# Revit family: ledlima_l15-36w-4000-dali-em1_549004003100
name_source: partatom
category: Leuchten
revit_build: Autodesk Revit 2016 (Build: 20190508_0715(x64)
units: mm (PartAtom-declared; Revit-internal decimal feet)

## family parameters
Basisbauteil = Fläche
Beim Laden mit Abzugskörper schneiden = Nein
Bemaßung runder Anschluss = Durchmesser verwenden
Gemeinsam genutzt = Nein
Lichtquelle = Nein
Raumberechnungspunkt = Nein
Teiletyp = Normal

## types (1)
- LEDLima L15-36W-4000-DALI-EM1 (1 x LED, 4140 lm)
    Approval mark = CE, ENEC
    Beschreibung = Stylish linear luminaire with high quality aluminum housing, suitable for surface mounting and suspended use. Suitable for use in office. Suspension kit including transparent cable as accessory. Connection kit accessory to create continuous lines available.
    CIE Flux Codes = 68 91 98 100 100
    Control Gear = Electronic ballast
    Height = 70 mm
    Hersteller = OPPLE
    Lamp Light Flux = 4140 lm
    Lamp count = 1
    Lampe = 1 x LED
    Length = 1500 mm
    Luminous efficacy = 115 lm/W
    ModVariant = Nein
    Modell = 549004003100
    Mounting Place = Ceiling
    Mounting Type = Pendant
    Number of Poles = 1
    OnlyDefault = Ja
    Power Factor = 1
    Product Name = LEDLima L15-36W-4000-DALI-EM1
    Product group = Lima
    ProductGroupID = 910
    Protection Class = Protection class I
    Protection Degree = IP 20
    RLX_Detail_Level = 1
    RlxData = <blob elided: 79281 chars, md5=f5207a1d>
    Scheinlast = 36 VA
    Socket = socket
    Standby Power = 0 W
    System Light Flux = 4140 lm
    System Power = 36 W
    Typenbild = 549004003100.jpg
    Typenkommentare = Product without accessories
    URL = http://relux.com
    VarID = ---
    Voltage = 0 V
    Vorgabe-Ansicht = 1800 mm
    Weight = 0.00 kg
    Width = 70 mm

## geometry (parser evidence)
native form markers: Blend x4, Sweep x9
no freeform markers — native parametric forms only
